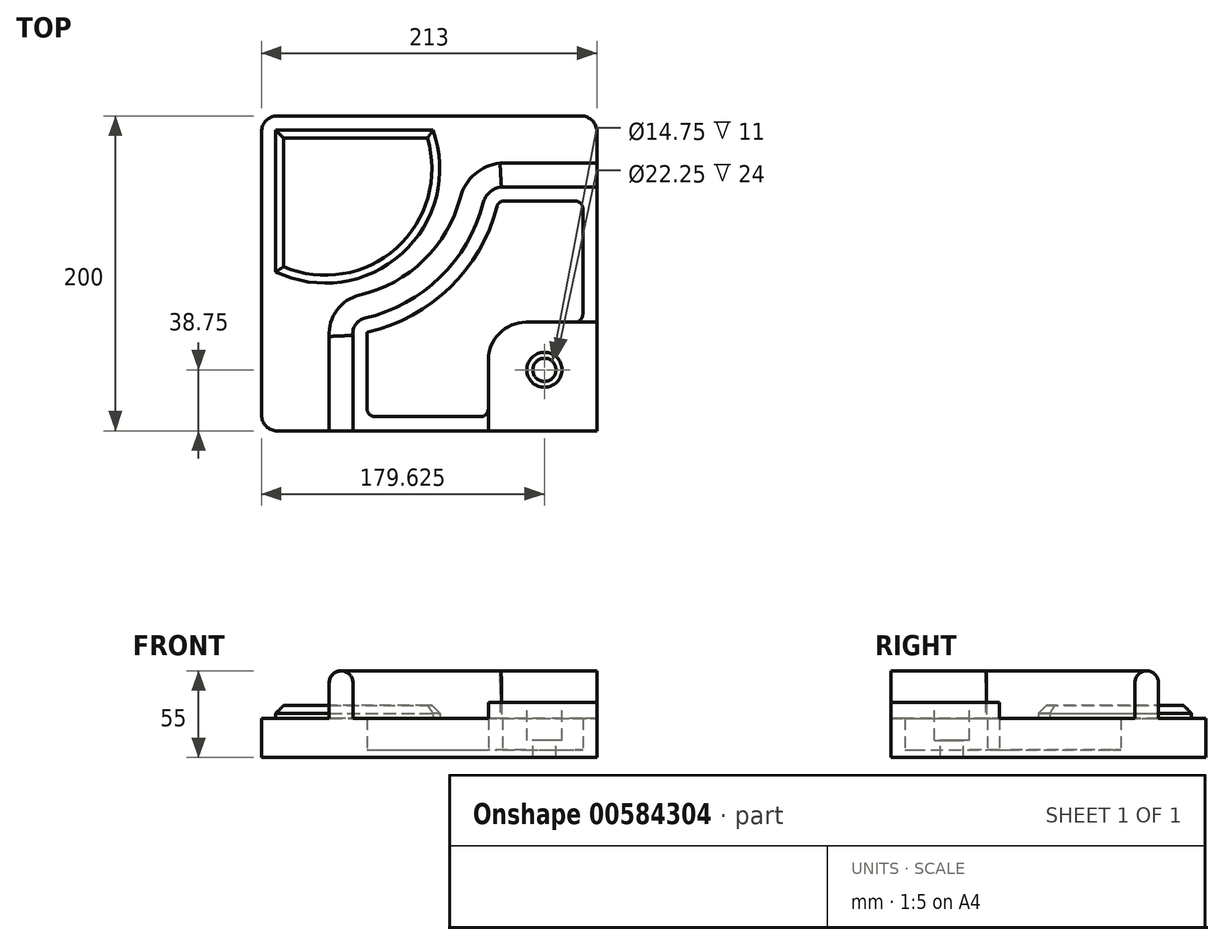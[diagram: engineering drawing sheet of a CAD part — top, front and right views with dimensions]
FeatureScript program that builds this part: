
annotation { "Feature Type Name" : "Feature", "Feature Type Description" : "" }
export const myFeature = defineFeature(function(context is Context, id is Id, definition is map)
    precondition{}
    {
        {
            var Q0;
            Q0=qCreatedBy(makeId("Top.planeOp"),FACE);
            var sketch = newSketch(context, id + "F0", { "sketchPlane" : qUnion([Q0])});
            skLineSegment(sketch, "E0.bottom", {"start": v(0, 0) * mm, "end": v(-213, 0) * mm});
            skLineSegment(sketch, "E0.top", {"start": v(0, 200) * mm, "end": v(-213, 200) * mm});
            skLineSegment(sketch, "E0.left", {"start": v(0, 0) * mm, "end": v(0, 200) * mm});
            skLineSegment(sketch, "E0.right", {"start": v(-213, 0) * mm, "end": v(-213, 200) * mm});
            skLineSegment(sketch, "E1.bottom", {"start": v(0, 0) * mm, "end": v(-170, 0) * mm});
            skLineSegment(sketch, "E1.top", {"start": v(0, 170) * mm, "end": v(-69, 170) * mm});
            skLineSegment(sketch, "E1.left", {"start": v(0, 0) * mm, "end": v(0, 170) * mm});
            skLineSegment(sketch, "E1.right", {"start": v(-170, 0) * mm, "end": v(-170, 60) * mm});
            skLineSegment(sketch, "E2", {"start": v(-155, 0) * mm, "end": v(-155, 60) * mm});
            skLineSegment(sketch, "E3", {"start": v(0, 155) * mm, "end": v(-60, 155) * mm});
            skPoint(sketch, "E4.visualSharp", {"position": v(-170, 170) * mm});
            skLineSegment(sketch, "E5", {"start": v(-170, 80) * mm, "end": v(-170, 80) * mm});
            skPoint(sketch, "E6.visualSharp", {"position": v(-80, 80) * mm});
            skLineSegment(sketch, "E7.bottom", {"start": v(0, 0) * mm, "end": v(-60, 0) * mm});
            skLineSegment(sketch, "E7.top", {"start": v(0, 60) * mm, "end": v(-45, 60) * mm});
            skLineSegment(sketch, "E7.left", {"start": v(0, 0) * mm, "end": v(0, 60) * mm});
            skLineSegment(sketch, "E7.right", {"start": v(-60, 0) * mm, "end": v(-60, 45) * mm});
            skPoint(sketch, "E8.centerSnap0", {"position": v(0, 30) * mm});
            skPoint(sketch, "E8.centerSnap1", {"position": v(-30, 0) * mm});
            skPoint(sketch, "E9.visualSharp", {"position": v(-60, 60) * mm});
            skArc(sketch, "E9.filletArc", {"start": v(-45, 60) * mm, "mid": v(-55.6, 55.6) * mm, "end": v(-60, 45) * mm});
            skPoint(sketch, "E10", {"position": v(-170, 64.04) * mm});
            skPoint(sketch, "E11", {"position": v(-170, 80) * mm});
            skPoint(sketch, "E12", {"position": v(-170, 89) * mm});
            skPoint(sketch, "E13", {"position": v(-89, 170) * mm});
            skPoint(sketch, "E14", {"position": v(-84, 170) * mm});
            skPoint(sketch, "E15", {"position": v(-65, 170) * mm});
            skLineSegment(sketch, "E16.bottom", {"start": v(-170, 0) * mm, "end": v(-146, 0) * mm, "construction": true});
            skLineSegment(sketch, "E16.top", {"start": v(-170, 9) * mm, "end": v(-146, 9) * mm, "construction": true});
            skLineSegment(sketch, "E16.left", {"start": v(-170, 0) * mm, "end": v(-170, 9) * mm, "construction": true});
            skLineSegment(sketch, "E16.right", {"start": v(-146, 0) * mm, "end": v(-146, 9) * mm, "construction": true});
            skLineSegment(sketch, "E17.bottom", {"start": v(-141, 9) * mm, "end": v(-74, 9) * mm});
            skLineSegment(sketch, "E17.left", {"start": v(-146, 14) * mm, "end": v(-146, 51) * mm});
            skLineSegment(sketch, "E17.right", {"start": v(-69, 14) * mm, "end": v(-69, 45) * mm});
            skLineSegment(sketch, "E18.bottom", {"start": v(-59.86, 146) * mm, "end": v(-13.87, 146) * mm});
            skLineSegment(sketch, "E18.top", {"start": v(-45, 69) * mm, "end": v(-14, 69) * mm});
            skLineSegment(sketch, "E18.right", {"start": v(-8.87, 141) * mm, "end": v(-9, 74) * mm});
            skLineSegment(sketch, "E19.top", {"start": v(-145, 80.04) * mm, "end": v(-145, 80.04) * mm});
            skLineSegment(sketch, "E19.left", {"start": v(-170, 60) * mm, "end": v(-170, 60) * mm});
            skPoint(sketch, "E20.visualSharp", {"position": v(-170, 80.04) * mm});
            skPoint(sketch, "E21.orphan", {"position": v(-69, 170) * mm});
            skLineSegment(sketch, "E22.bottom", {"start": v(-213, 200) * mm, "end": v(-204, 200) * mm, "construction": true});
            skLineSegment(sketch, "E22.top", {"start": v(-213, 191) * mm, "end": v(-204, 191) * mm, "construction": true});
            skLineSegment(sketch, "E22.left", {"start": v(-213, 200) * mm, "end": v(-213, 191) * mm, "construction": true});
            skLineSegment(sketch, "E22.right", {"start": v(-204, 200) * mm, "end": v(-204, 191) * mm, "construction": true});
            skArc(sketch, "E23", {"start": v(-150.68, 86.2) * mm, "mid": v(-108.55, 109.84) * mm, "end": v(-85.8, 152.46) * mm});
            skArc(sketch, "E24", {"start": v(-150.68, 86.2) * mm, "mid": v(-165.19, 76.67) * mm, "end": v(-170, 60) * mm});
            skArc(sketch, "E25.trimOffspring", {"start": v(-169.02, 69) * mm, "mid": v(-169.5, 69) * mm, "end": v(-170, 69) * mm});
            skPoint(sketch, "E26.end.orphan", {"position": v(-60, 170) * mm});
            skArc(sketch, "E27", {"start": v(-69, 170) * mm, "mid": v(-79.45, 163.19) * mm, "end": v(-85.8, 152.46) * mm});
            skArc(sketch, "E28.0", {"start": v(-147.31, 71.58) * mm, "mid": v(-153.12, 67.77) * mm, "end": v(-155.04, 61.1) * mm});
            skArc(sketch, "E29.0", {"start": v(-147.31, 71.58) * mm, "mid": v(-98.58, 98.58) * mm, "end": v(-71.58, 147.31) * mm});
            skArc(sketch, "E30.0", {"start": v(-65.82, 155) * mm, "mid": v(-69.57, 151.7) * mm, "end": v(-71.72, 147.18) * mm});
            skLineSegment(sketch, "E31", {"start": v(-65.82, 155) * mm, "end": v(-60, 155) * mm});
            skArc(sketch, "E32.0", {"start": v(-145.3, 62.81) * mm, "mid": v(-145.95, 62.3) * mm, "end": v(-146, 61.48) * mm});
            skLineSegment(sketch, "E33", {"start": v(-155.04, 61.1) * mm, "end": v(-155, 60) * mm});
            skLineSegment(sketch, "E34", {"start": v(-146, 61.1) * mm, "end": v(-146, 61.48) * mm});
            skLineSegment(sketch, "E35", {"start": v(-146, 61.1) * mm, "end": v(-146, 51) * mm});
            skArc(sketch, "E36.0", {"start": v(-145.3, 62.81) * mm, "mid": v(-93.28, 91.17) * mm, "end": v(-63.52, 142.4) * mm});
            skArc(sketch, "E37.0", {"start": v(-45, 69) * mm, "mid": v(-61.97, 61.97) * mm, "end": v(-69, 45) * mm});
            skPoint(sketch, "E38.visualSharp", {"position": v(-146, 9) * mm});
            skArc(sketch, "E38.filletArc", {"start": v(-146, 14) * mm, "mid": v(-144.54, 10.46) * mm, "end": v(-141, 9) * mm});
            skPoint(sketch, "E39.visualSharp", {"position": v(-69, 9) * mm});
            skArc(sketch, "E39.filletArc", {"start": v(-74, 9) * mm, "mid": v(-70.46, 10.46) * mm, "end": v(-69, 14) * mm});
            skPoint(sketch, "E40.visualSharp", {"position": v(-9, 69) * mm});
            skArc(sketch, "E40.filletArc", {"start": v(-14, 69) * mm, "mid": v(-10.46, 70.46) * mm, "end": v(-9, 74) * mm});
            skPoint(sketch, "E41.visualSharp", {"position": v(-8.86, 146) * mm});
            skArc(sketch, "E41.filletArc", {"start": v(-8.87, 141) * mm, "mid": v(-10.33, 144.53) * mm, "end": v(-13.87, 146) * mm});
            skLineSegment(sketch, "E42", {"start": v(-59.9, 146) * mm, "end": v(-59.86, 146) * mm});
            skPoint(sketch, "E43.visualSharp", {"position": v(-62.82, 145.26) * mm});
            skArc(sketch, "E43.filletArc", {"start": v(-59.9, 146) * mm, "mid": v(-62.2, 144.7) * mm, "end": v(-63.52, 142.4) * mm});
            skPoint(sketch, "E44.end.orphan", {"position": v(-170, 84) * mm});
            skPoint(sketch, "E8.center.orphan", {"position": v(-30, 30) * mm});
            skSolve(sketch);
        }
        {
            var Q0;
            Q0 = qSketchRegion(id + "F0", true);
            extrude(context, id + "F1", {"entities" : qUnion([Q0]), "depth" : 25 * mm, "offsetDistance" : 25 * mm});
        }
        {
            var Q0;
            Q0=makeQuery(id+"F1.opExtrude","CAP_FACE",FACE,{"disambiguationData":[OSD([sQuery(id+"F0.wireOp",EDGE,"E0.bottom"),sQuery(id+"F0.wireOp",EDGE,"E0.top"),sQuery(id+"F0.wireOp",EDGE,"E0.left"),sQuery(id+"F0.wireOp",EDGE,"E0.right"),sQuery(id+"F0.wireOp",EDGE,"E1.bottom"),sQuery(id+"F0.wireOp",EDGE,"E1.left"),sQuery(id+"F0.wireOp",EDGE,"E7.bottom"),sQuery(id+"F0.wireOp",EDGE,"E7.left"),sQuery(id+"F0.wireOp",EDGE,"E17.bottom"),sQuery(id+"F0.wireOp",EDGE,"E17.left"),sQuery(id+"F0.wireOp",EDGE,"E17.right"),sQuery(id+"F0.wireOp",EDGE,"E18.bottom"),sQuery(id+"F0.wireOp",EDGE,"E18.top"),sQuery(id+"F0.wireOp",EDGE,"E18.right"),sQuery(id+"F0.wireOp",EDGE,"E32.0"),sQuery(id+"F0.wireOp",EDGE,"E34"),sQuery(id+"F0.wireOp",EDGE,"E35"),sQuery(id+"F0.wireOp",EDGE,"E36.0"),sQuery(id+"F0.wireOp",EDGE,"E37.0"),sQuery(id+"F0.wireOp",EDGE,"E38.filletArc"),sQuery(id+"F0.wireOp",EDGE,"E39.filletArc"),sQuery(id+"F0.wireOp",EDGE,"E40.filletArc"),sQuery(id+"F0.wireOp",EDGE,"E41.filletArc"),sQuery(id+"F0.wireOp",EDGE,"E42"),sQuery(id+"F0.wireOp",EDGE,"E43.filletArc")])],"isStart":false});
            var sketch = newSketch(context, id + "F2", { "sketchPlane" : qUnion([Q0])});
            skPoint(sketch, "E45", {"position": v(-33.38, 38.75) * mm});
            skSolve(sketch);
        }
        {
            var Q0;
            Q0=sQuery(id+"F2.wireOp",VERTEX,"E45");
            var Q1;
            Q1=makeQuery(id+"F1.opExtrude","SWEPT_BODY",BODY,{"disambiguationData":[OSD([sQuery(id+"F0.wireOp",EDGE,"E0.bottom"),sQuery(id+"F0.wireOp",EDGE,"E0.top"),sQuery(id+"F0.wireOp",EDGE,"E0.left"),sQuery(id+"F0.wireOp",EDGE,"E0.right"),sQuery(id+"F0.wireOp",EDGE,"E1.bottom"),sQuery(id+"F0.wireOp",EDGE,"E1.left"),sQuery(id+"F0.wireOp",EDGE,"E7.bottom"),sQuery(id+"F0.wireOp",EDGE,"E7.left"),sQuery(id+"F0.wireOp",EDGE,"E17.bottom"),sQuery(id+"F0.wireOp",EDGE,"E17.left"),sQuery(id+"F0.wireOp",EDGE,"E17.right"),sQuery(id+"F0.wireOp",EDGE,"E18.bottom"),sQuery(id+"F0.wireOp",EDGE,"E18.top"),sQuery(id+"F0.wireOp",EDGE,"E18.right"),sQuery(id+"F0.wireOp",EDGE,"E32.0"),sQuery(id+"F0.wireOp",EDGE,"E34"),sQuery(id+"F0.wireOp",EDGE,"E35"),sQuery(id+"F0.wireOp",EDGE,"E36.0"),sQuery(id+"F0.wireOp",EDGE,"E37.0"),sQuery(id+"F0.wireOp",EDGE,"E38.filletArc"),sQuery(id+"F0.wireOp",EDGE,"E39.filletArc"),sQuery(id+"F0.wireOp",EDGE,"E40.filletArc"),sQuery(id+"F0.wireOp",EDGE,"E41.filletArc"),sQuery(id+"F0.wireOp",EDGE,"E42"),sQuery(id+"F0.wireOp",EDGE,"E43.filletArc")])]});
            hole(context, id + "F3", {"style" : HoleStyle.C_BORE, "endStyle" : HoleEndStyle.THROUGH, "standardTappedOrClearance" : lookupTablePath({ "standard" : "ISO", "fit" : "Close", "size" : "M14", "type" : "Clearance" }), "standardBlindInLast" : lookupTablePath({ "fit" : "Close", "standard" : "ISO", "size" : "M14", "type" : "Clearance" }), "holeDiameter" : 14.75 * mm, "cBoreDiameter" : 22.25 * mm, "cBoreDepth" : 14 * mm, "majorDiameter" : 5 * mm, "isTappedThrough" : true, "tappedDepth" : 12 * mm, "tapClearance" : 3, "locations" : qUnion([Q0]), "scope" : qUnion([Q1])});
        }
        {
            var Q0;
            Q0=makeQuery(id+"F1.opExtrude","SWEPT_EDGE",EDGE,{"disambiguationData":[OSD([sQuery(id+"F0.wireOp",EDGE,"E7.bottom"),sQuery(id+"F0.wireOp",EDGE,"E7.left")])]});
            var Q1;
            Q1=makeQuery(id+"F1.opExtrude","SWEPT_EDGE",EDGE,{"disambiguationData":[OSD([sQuery(id+"F0.wireOp",EDGE,"E0.bottom"),sQuery(id+"F0.wireOp",EDGE,"E0.right")])]});
            var Q2;
            Q2=makeQuery(id+"F1.opExtrude","SWEPT_EDGE",EDGE,{"disambiguationData":[OSD([sQuery(id+"F0.wireOp",EDGE,"E0.top"),sQuery(id+"F0.wireOp",EDGE,"E0.right")])]});
            var Q3;
            Q3=makeQuery(id+"F1.opExtrude","SWEPT_EDGE",EDGE,{"disambiguationData":[OSD([sQuery(id+"F0.wireOp",EDGE,"E0.top"),sQuery(id+"F0.wireOp",EDGE,"E0.left")])]});
            fillet(context, id + "F4", {"entities" : qUnion([Q0, Q1, Q2, Q3]), "radius" : 10 * mm, "tangentPropagation" : true, "allowEdgeOverflow" : false});
        }
        {
            var Q0;
            Q0=makeQuery(id+"F1.opExtrude","CAP_FACE",FACE,{"disambiguationData":[OSD([sQuery(id+"F0.wireOp",EDGE,"E0.bottom"),sQuery(id+"F0.wireOp",EDGE,"E0.top"),sQuery(id+"F0.wireOp",EDGE,"E0.left"),sQuery(id+"F0.wireOp",EDGE,"E0.right"),sQuery(id+"F0.wireOp",EDGE,"E1.bottom"),sQuery(id+"F0.wireOp",EDGE,"E1.left"),sQuery(id+"F0.wireOp",EDGE,"E7.bottom"),sQuery(id+"F0.wireOp",EDGE,"E7.left"),sQuery(id+"F0.wireOp",EDGE,"E17.bottom"),sQuery(id+"F0.wireOp",EDGE,"E17.left"),sQuery(id+"F0.wireOp",EDGE,"E17.right"),sQuery(id+"F0.wireOp",EDGE,"E18.bottom"),sQuery(id+"F0.wireOp",EDGE,"E18.top"),sQuery(id+"F0.wireOp",EDGE,"E18.right"),sQuery(id+"F0.wireOp",EDGE,"E32.0"),sQuery(id+"F0.wireOp",EDGE,"E34"),sQuery(id+"F0.wireOp",EDGE,"E35"),sQuery(id+"F0.wireOp",EDGE,"E36.0"),sQuery(id+"F0.wireOp",EDGE,"E37.0"),sQuery(id+"F0.wireOp",EDGE,"E38.filletArc"),sQuery(id+"F0.wireOp",EDGE,"E39.filletArc"),sQuery(id+"F0.wireOp",EDGE,"E40.filletArc"),sQuery(id+"F0.wireOp",EDGE,"E41.filletArc"),sQuery(id+"F0.wireOp",EDGE,"E42"),sQuery(id+"F0.wireOp",EDGE,"E43.filletArc")])],"isStart":false});
            var sketch = newSketch(context, id + "F5", { "sketchPlane" : qUnion([Q0])});
            skLineSegment(sketch, "E46", {"start": v(-69, 14) * mm, "end": v(-69, 0) * mm});
            skLineSegment(sketch, "E47", {"start": v(-14, 69) * mm, "end": v(0, 69) * mm});
            skSolve(sketch);
        }
        {
            var Q0;
            Q0 = qSketchRegion(id + "F5", true);
            var Q1;
            {var subQ3=sQuery(id+"F5.wireOp",EDGE,"E46");Q1=makeQuery(id+"F5.imprint","IMPRINT",FACE,{"disambiguationData":[TD([[makeQuery(id+"F5.imprint","IMPRINT",EDGE,{"derivedFrom":subQ3}),1.0]])]});}
            extrude(context, id + "F6", {"entities" : qUnion([Q0, Q1]), "operationType" : NewBodyOperationType.ADD, "depth" : 10 * mm, "offsetDistance" : 25 * mm});
        }
        {
            var Q0;
            Q0=makeQuery(id+"F1.opExtrude","CAP_FACE",FACE,{"disambiguationData":[OSD([sQuery(id+"F0.wireOp",EDGE,"E0.bottom"),sQuery(id+"F0.wireOp",EDGE,"E0.top"),sQuery(id+"F0.wireOp",EDGE,"E0.left"),sQuery(id+"F0.wireOp",EDGE,"E0.right"),sQuery(id+"F0.wireOp",EDGE,"E1.bottom"),sQuery(id+"F0.wireOp",EDGE,"E1.left"),sQuery(id+"F0.wireOp",EDGE,"E7.bottom"),sQuery(id+"F0.wireOp",EDGE,"E7.left"),sQuery(id+"F0.wireOp",EDGE,"E17.bottom"),sQuery(id+"F0.wireOp",EDGE,"E17.left"),sQuery(id+"F0.wireOp",EDGE,"E17.right"),sQuery(id+"F0.wireOp",EDGE,"E18.bottom"),sQuery(id+"F0.wireOp",EDGE,"E18.top"),sQuery(id+"F0.wireOp",EDGE,"E18.right"),sQuery(id+"F0.wireOp",EDGE,"E32.0"),sQuery(id+"F0.wireOp",EDGE,"E34"),sQuery(id+"F0.wireOp",EDGE,"E35"),sQuery(id+"F0.wireOp",EDGE,"E36.0"),sQuery(id+"F0.wireOp",EDGE,"E37.0"),sQuery(id+"F0.wireOp",EDGE,"E38.filletArc"),sQuery(id+"F0.wireOp",EDGE,"E39.filletArc"),sQuery(id+"F0.wireOp",EDGE,"E40.filletArc"),sQuery(id+"F0.wireOp",EDGE,"E41.filletArc"),sQuery(id+"F0.wireOp",EDGE,"E42"),sQuery(id+"F0.wireOp",EDGE,"E43.filletArc")])],"isStart":false});
            var sketch = newSketch(context, id + "F7", { "sketchPlane" : qUnion([Q0])});
            skArc(sketch, "E48.0", {"start": v(-147.31, 71.58) * mm, "mid": v(-99.56, 97.62) * mm, "end": v(-72.23, 144.65) * mm});
            skLineSegment(sketch, "E49.0", {"start": v(-60.66, 155) * mm, "end": v(-13.87, 155) * mm});
            skArc(sketch, "E50.0", {"start": v(-60.66, 155) * mm, "mid": v(-68.01, 151.58) * mm, "end": v(-72.23, 144.65) * mm});
            skLineSegment(sketch, "E51.0", {"start": v(-155, 14) * mm, "end": v(-155, 60.68) * mm});
            skLineSegment(sketch, "E52", {"start": v(-13.87, 155) * mm, "end": v(0, 155) * mm});
            skLineSegment(sketch, "E53", {"start": v(-155, 14) * mm, "end": v(-155, 0) * mm});
            skArc(sketch, "E54.0", {"start": v(-147.31, 71.58) * mm, "mid": v(-153.24, 67.6) * mm, "end": v(-155, 60.68) * mm});
            skArc(sketch, "E55.0", {"start": v(-61.54, 170) * mm, "mid": v(-77.54, 163.17) * mm, "end": v(-86.75, 148.42) * mm});
            skLineSegment(sketch, "E55.1", {"start": v(-170, 14) * mm, "end": v(-170, 0) * mm});
            skLineSegment(sketch, "E55.2", {"start": v(-170, 14) * mm, "end": v(-170, 60) * mm});
            skArc(sketch, "E55.3", {"start": v(-150.68, 86.2) * mm, "mid": v(-165.19, 76.67) * mm, "end": v(-170, 60) * mm});
            skArc(sketch, "E55.4", {"start": v(-150.68, 86.2) * mm, "mid": v(-110.02, 108.37) * mm, "end": v(-86.75, 148.42) * mm});
            skLineSegment(sketch, "E56.0", {"start": v(-61.54, 170) * mm, "end": v(-13.87, 170) * mm});
            skLineSegment(sketch, "E57.0", {"start": v(-13.87, 170) * mm, "end": v(0, 170) * mm});
            skSolve(sketch);
        }
        {
            var Q0;
            Q0=makeQuery(id+"F7.imprint","IMPRINT",FACE,{"disambiguationData":[TD([[makeQuery(id+"F7.imprint","IMPRINT",EDGE,{"derivedFrom":sQuery(id+"F7.wireOp",EDGE,"E48.0")}),1.0]])]});
            extrude(context, id + "F8", {"entities" : qUnion([Q0]), "operationType" : NewBodyOperationType.ADD, "depth" : 30 * mm, "offsetDistance" : 25 * mm});
        }
        {
            var Q0;
            Q0=makeQuery(id+"F8.opExtrude","CAP_EDGE",EDGE,{"disambiguationData":[OSD([sQuery(id+"F7.wireOp",EDGE,"E55.1"),sQuery(id+"F7.wireOp",EDGE,"E55.2")])],"isStart":false});
            var Q1;
            Q1=makeQuery(id+"F8.opExtrude","CAP_EDGE",EDGE,{"disambiguationData":[OSD([sQuery(id+"F7.wireOp",EDGE,"E55.4")])],"isStart":false});
            var Q2;
            Q2=makeQuery(id+"F8.opExtrude","CAP_EDGE",EDGE,{"disambiguationData":[OSD([sQuery(id+"F7.wireOp",EDGE,"E55.3")])],"isStart":false});
            var Q3;
            Q3=makeQuery(id+"F8.opExtrude","CAP_EDGE",EDGE,{"disambiguationData":[OSD([sQuery(id+"F7.wireOp",EDGE,"E48.0")])],"isStart":false});
            var Q4;
            Q4=makeQuery(id+"F8.opExtrude","CAP_EDGE",EDGE,{"disambiguationData":[OSD([sQuery(id+"F7.wireOp",EDGE,"E51.0"),sQuery(id+"F7.wireOp",EDGE,"E53")])],"isStart":false});
            var Q5;
            Q5=makeQuery(id+"F8.opExtrude","CAP_EDGE",EDGE,{"disambiguationData":[OSD([sQuery(id+"F7.wireOp",EDGE,"E54.0")])],"isStart":false});
            var Q6;
            Q6=makeQuery(id+"F8.opExtrude","CAP_EDGE",EDGE,{"disambiguationData":[OSD([sQuery(id+"F7.wireOp",EDGE,"E49.0"),sQuery(id+"F7.wireOp",EDGE,"E52")])],"isStart":false});
            var Q7;
            Q7=makeQuery(id+"F8.opExtrude","CAP_EDGE",EDGE,{"disambiguationData":[OSD([sQuery(id+"F7.wireOp",EDGE,"E56.0"),sQuery(id+"F7.wireOp",EDGE,"E57.0")])],"isStart":false});
            var Q8;
            Q8=makeQuery(id+"F8.opExtrude","CAP_EDGE",EDGE,{"disambiguationData":[OSD([sQuery(id+"F7.wireOp",EDGE,"E50.0")])],"isStart":false});
            fillet(context, id + "F9", {"entities" : qUnion([Q0, Q1, Q2, Q3, Q4, Q5, Q6, Q7, Q8]), "radius" : 7.5 * mm, "tangentPropagation" : true, "allowEdgeOverflow" : false});
        }
        {
            var Q0;
            {var subQ0=sQuery(id+"F0.wireOp",EDGE,"E0.left");var subQ1=sQuery(id+"F0.wireOp",EDGE,"E0.top");var subQ2=sQuery(id+"F0.wireOp",EDGE,"E0.right");var subQ3=sQuery(id+"F0.wireOp",EDGE,"E0.bottom");var subQ4=sQuery(id+"F0.wireOp",EDGE,"E7.bottom");var subQ5=sQuery(id+"F0.wireOp",EDGE,"E1.bottom");var subQ6=sQuery(id+"F0.wireOp",EDGE,"E7.left");var subQ7=sQuery(id+"F0.wireOp",EDGE,"E1.left");Q0=makeQuery(id+"F8.boolean.opBoolean","SPLIT",FACE,{"disambiguationData":[TD([makeQuery(id+"F1.opExtrude","SWEPT_FACE",FACE,{"disambiguationData":[OSD([subQ1])]})])],"derivedFrom":makeQuery(id+"F1.opExtrude","CAP_FACE",FACE,{"disambiguationData":[OSD([subQ3,subQ1,subQ0,subQ2,subQ5,subQ7,subQ4,subQ6,sQuery(id+"F0.wireOp",EDGE,"E17.bottom"),sQuery(id+"F0.wireOp",EDGE,"E17.left"),sQuery(id+"F0.wireOp",EDGE,"E17.right"),sQuery(id+"F0.wireOp",EDGE,"E18.bottom"),sQuery(id+"F0.wireOp",EDGE,"E18.top"),sQuery(id+"F0.wireOp",EDGE,"E18.right"),sQuery(id+"F0.wireOp",EDGE,"E32.0"),sQuery(id+"F0.wireOp",EDGE,"E34"),sQuery(id+"F0.wireOp",EDGE,"E35"),sQuery(id+"F0.wireOp",EDGE,"E36.0"),sQuery(id+"F0.wireOp",EDGE,"E37.0"),sQuery(id+"F0.wireOp",EDGE,"E38.filletArc"),sQuery(id+"F0.wireOp",EDGE,"E39.filletArc"),sQuery(id+"F0.wireOp",EDGE,"E40.filletArc"),sQuery(id+"F0.wireOp",EDGE,"E41.filletArc"),sQuery(id+"F0.wireOp",EDGE,"E42"),sQuery(id+"F0.wireOp",EDGE,"E43.filletArc")])],"isStart":false})});}
            var sketch = newSketch(context, id + "F10", { "sketchPlane" : qUnion([Q0])});
            skLineSegment(sketch, "E58", {"start": v(-204, 191) * mm, "end": v(-204, 101) * mm});
            skLineSegment(sketch, "E59", {"start": v(-204, 191) * mm, "end": v(-104, 191) * mm});
            skPoint(sketch, "E60", {"position": v(-170, 170) * mm});
            skLineSegment(sketch, "E61.0", {"start": v(0, 170) * mm, "end": v(0, 190) * mm});
            skLineSegment(sketch, "E62.0", {"start": v(-170, 0) * mm, "end": v(-203, 0) * mm});
            skArc(sketch, "E63", {"start": v(-204, 101) * mm, "mid": v(-123.88, 112.53) * mm, "end": v(-104, 191) * mm});
            skSolve(sketch);
        }
        {
            var Q0;
            Q0=makeQuery(id+"F10.imprint","IMPRINT",FACE,{"disambiguationData":[TD([[makeQuery(id+"F10.imprint","IMPRINT",EDGE,{"derivedFrom":sQuery(id+"F10.wireOp",EDGE,"E58")}),1.0]])]});
            extrude(context, id + "F11", {"entities" : qUnion([Q0]), "operationType" : NewBodyOperationType.ADD, "depth" : 8 * mm, "offsetDistance" : 25 * mm});
        }
        {
            var Q0;
            Q0=makeQuery(id+"F11.opExtrude","CAP_FACE",FACE,{"disambiguationData":[OSD([sQuery(id+"F10.wireOp",EDGE,"E58"),sQuery(id+"F10.wireOp",EDGE,"E59"),sQuery(id+"F10.wireOp",EDGE,"E63")])],"isStart":false});
            chamfer(context, id + "F12", {"entities" : qUnion([Q0]), "chamferType" : ChamferType.OFFSET_ANGLE, "width" : 5 * mm, "oppositeDirection" : false, "angle" : 45 * degree, "tangentPropagation" : true});
        }
        {
            var Q0;
            Q0=makeQuery(id+"F0.imprint","IMPRINT",FACE,{"disambiguationData":[TD([[makeQuery(id+"F0.imprint","IMPRINT",EDGE,{"derivedFrom":sQuery(id+"F0.wireOp",EDGE,"E17.bottom")}),1.0]])]});
            extrude(context, id + "F13", {"entities" : qUnion([Q0]), "operationType" : NewBodyOperationType.ADD, "depth" : 5 * mm, "offsetDistance" : 25 * mm});
        }
    });
